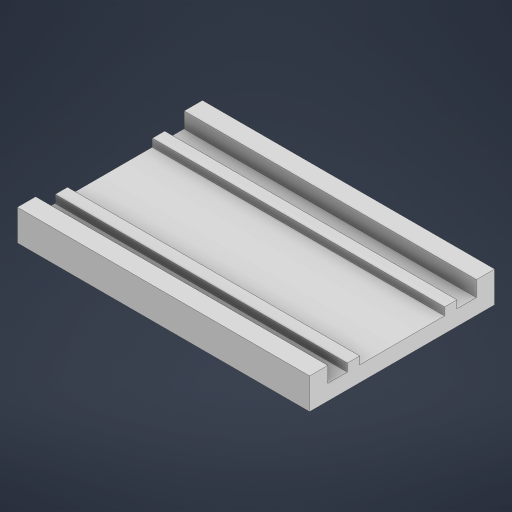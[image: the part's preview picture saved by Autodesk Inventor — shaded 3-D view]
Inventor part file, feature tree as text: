
AUTODESK INVENTOR PART (.ipt)
format: ipt  version: 2024 (Build 280153000, 153)  size: 221,184 bytes
history: native  units: in
note: dims shown in document units (in); Inventor stores cm internally (conversion verified against a paired STEP export)
features: extrude x3, sketch x3
ambient origin geometry x8: Origin, YZ Plane, XZ Plane, XY Plane, X Axis, Y Axis, Z Axis, Center Point
bodies: Solid1 (feature_tree)
feature tree (6):
  extrude  "Extrusion1"  Depth=2.3622in
  extrude  "Extrusion2"  Depth=1.2008in
  extrude  "Extrusion3"  Depth=0.1in
  sketch  "Sketch1"  dims[d0=1.4961in d1=2.3622in]
  sketch  "Sketch2"  dims[d2=0.25in d3=0.0in d4=1.2008in]
  sketch  "Sketch3"  dims[d5=0.125in d6=0.0in d7=0.1in d8=0.1in d9=0.8858in d10=0.4429in d11=0.0625in d12=0.0in]
